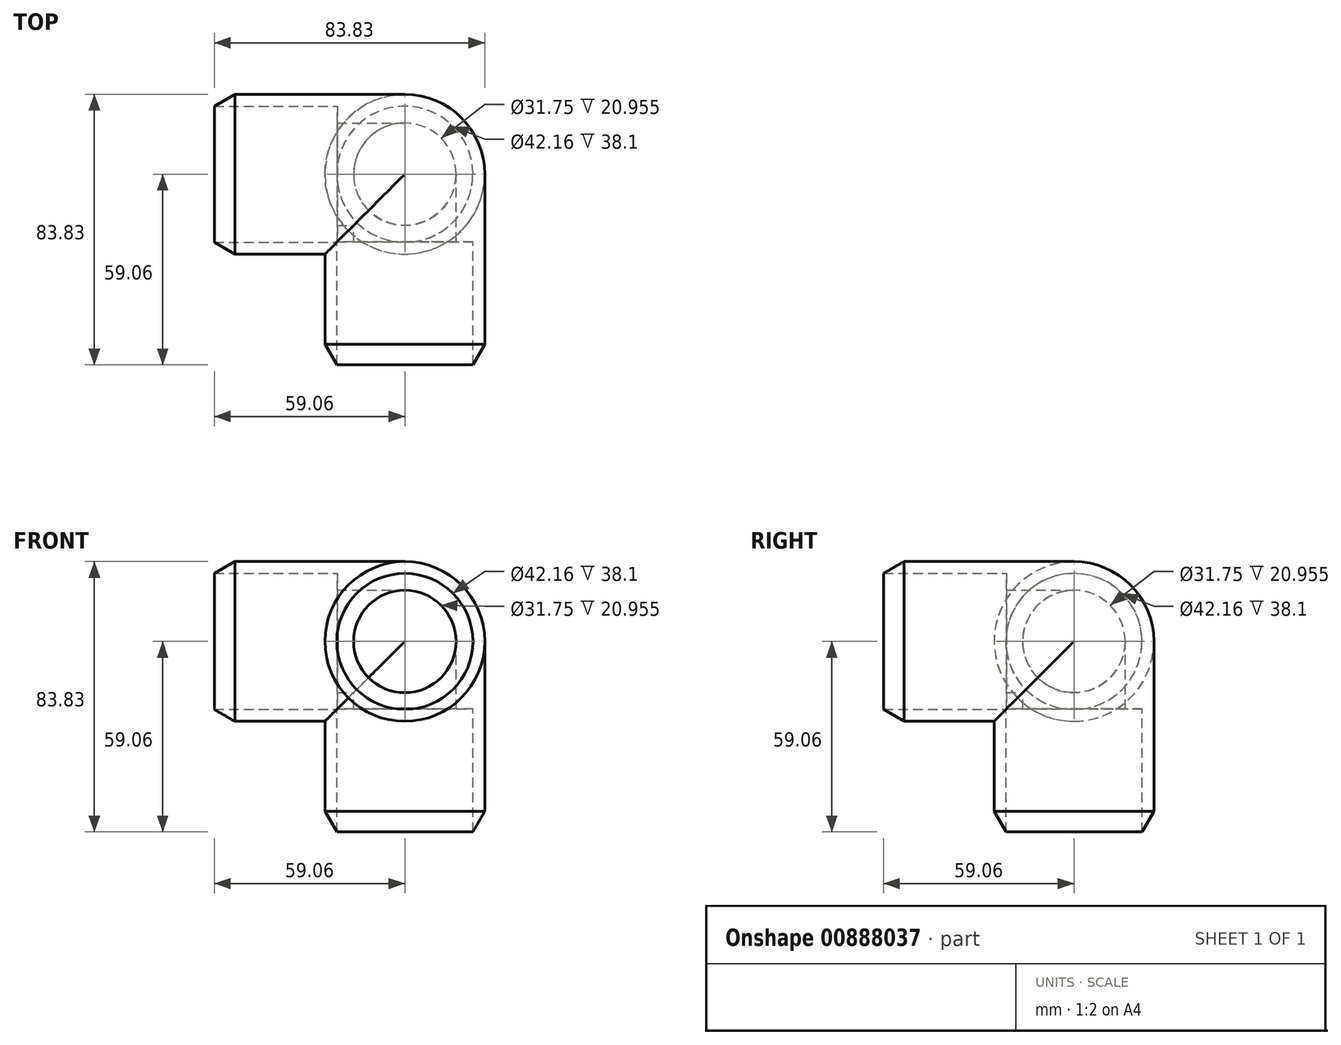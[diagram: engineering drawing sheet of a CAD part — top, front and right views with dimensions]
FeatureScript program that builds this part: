
annotation { "Feature Type Name" : "Feature", "Feature Type Description" : "" }
export const myFeature = defineFeature(function(context is Context, id is Id, definition is map)
    precondition{}
    {
        {
            var Q0;
            Q0=qCreatedBy(makeId("Right.planeOp"),FACE);
            var sketch = newSketch(context, id + "F0", { "sketchPlane" : qUnion([Q0])});
            skLineSegment(sketch, "E0", {"start": v(-59.06, 21.08) * mm, "end": v(-20.96, 21.08) * mm});
            skLineSegment(sketch, "E1", {"start": v(-20.96, 21.08) * mm, "end": v(-20.96, 15.88) * mm});
            skLineSegment(sketch, "E2", {"start": v(-20.96, 15.88) * mm, "end": v(0, 15.88) * mm});
            skLineSegment(sketch, "E3", {"start": v(15.87, 0) * mm, "end": v(15.87, 0) * mm});
            skLineSegment(sketch, "E4", {"start": v(15.87, 0) * mm, "end": v(24.77, 0) * mm});
            skLineSegment(sketch, "E5", {"start": v(24.77, 0) * mm, "end": v(24.77, 0) * mm});
            skLineSegment(sketch, "E6", {"start": v(0, 24.77) * mm, "end": v(-52.68, 24.76) * mm});
            skLineSegment(sketch, "E7", {"start": v(-52.68, 24.76) * mm, "end": v(-59.06, 21.08) * mm});
            skArc(sketch, "E8.filletArc", {"start": v(24.77, 0) * mm, "mid": v(17.51, 17.51) * mm, "end": v(0, 24.77) * mm});
            skArc(sketch, "E9.filletArc", {"start": v(15.88, 0) * mm, "mid": v(11.23, 11.23) * mm, "end": v(0, 15.88) * mm});
            skLineSegment(sketch, "E10", {"start": v(0, 0) * mm, "end": v(0, -11.7) * mm});
            skLineSegment(sketch, "E11", {"start": v(0, 0) * mm, "end": v(10.52, 0) * mm});
            skLineSegment(sketch, "E12", {"start": v(-59.06, 21.08) * mm, "end": v(-59.06, 0) * mm});
            skLineSegment(sketch, "E13", {"start": v(-59.06, 0) * mm, "end": v(15.87, 0) * mm});
            skSolve(sketch);
        }
        {
            var Q0;
            Q0=qCreatedBy(makeId("Right.planeOp"),FACE);
            var sketch = newSketch(context, id + "F1", { "sketchPlane" : qUnion([Q0])});
            skLineSegment(sketch, "E14", {"start": v(-21.08, -59.06) * mm, "end": v(-21.08, -20.96) * mm});
            skLineSegment(sketch, "E15", {"start": v(-21.08, -20.96) * mm, "end": v(-15.88, -20.96) * mm});
            skLineSegment(sketch, "E16", {"start": v(-15.88, -20.96) * mm, "end": v(-15.88, 0) * mm});
            skLineSegment(sketch, "E17", {"start": v(0, 15.88) * mm, "end": v(0, 15.88) * mm});
            skLineSegment(sketch, "E18", {"start": v(0, 15.88) * mm, "end": v(0, 24.77) * mm});
            skLineSegment(sketch, "E19", {"start": v(0, 24.77) * mm, "end": v(0, 24.77) * mm});
            skLineSegment(sketch, "E20", {"start": v(-24.77, 0) * mm, "end": v(-24.76, -52.68) * mm});
            skLineSegment(sketch, "E21", {"start": v(-24.76, -52.68) * mm, "end": v(-21.08, -59.06) * mm});
            skArc(sketch, "E22.filletArc", {"start": v(0, 24.77) * mm, "mid": v(-17.51, 17.51) * mm, "end": v(-24.77, 0) * mm});
            skArc(sketch, "E23.filletArc", {"start": v(0, 15.88) * mm, "mid": v(-11.23, 11.23) * mm, "end": v(-15.88, 0) * mm});
            skLineSegment(sketch, "E24", {"start": v(0, 36.04) * mm, "end": v(0, 0) * mm});
            skLineSegment(sketch, "E25", {"start": v(-2.18, 0) * mm, "end": v(0, 0) * mm});
            skLineSegment(sketch, "E26", {"start": v(-21.08, -59.06) * mm, "end": v(0, -59.06) * mm});
            skLineSegment(sketch, "E27", {"start": v(0, -59.06) * mm, "end": v(0, 15.88) * mm});
            skSolve(sketch);
        }
        {
            var Q0;
            Q0=qCreatedBy(makeId("Top.planeOp"),FACE);
            var sketch = newSketch(context, id + "F2", { "sketchPlane" : qUnion([Q0])});
            skLineSegment(sketch, "E28", {"start": v(-59.06, 21.08) * mm, "end": v(-20.96, 21.08) * mm});
            skLineSegment(sketch, "E29", {"start": v(-20.96, 21.08) * mm, "end": v(-20.96, 15.88) * mm});
            skLineSegment(sketch, "E30", {"start": v(-20.96, 15.88) * mm, "end": v(0, 15.88) * mm});
            skLineSegment(sketch, "E31", {"start": v(15.88, 0) * mm, "end": v(15.88, 0) * mm});
            skLineSegment(sketch, "E32", {"start": v(15.88, 0) * mm, "end": v(24.77, 0) * mm});
            skLineSegment(sketch, "E33", {"start": v(24.77, 0) * mm, "end": v(24.77, 0) * mm});
            skLineSegment(sketch, "E34", {"start": v(0, 24.77) * mm, "end": v(-52.68, 24.76) * mm});
            skLineSegment(sketch, "E35", {"start": v(-52.68, 24.76) * mm, "end": v(-59.06, 21.08) * mm});
            skArc(sketch, "E36.filletArc", {"start": v(24.77, 0) * mm, "mid": v(17.51, 17.51) * mm, "end": v(0, 24.77) * mm});
            skArc(sketch, "E37.filletArc", {"start": v(15.88, 0) * mm, "mid": v(11.23, 11.23) * mm, "end": v(0, 15.88) * mm});
            skLineSegment(sketch, "E38", {"start": v(0, 15.42) * mm, "end": v(0, 0) * mm});
            skLineSegment(sketch, "E39", {"start": v(-12.56, 0) * mm, "end": v(0, 0) * mm});
            skLineSegment(sketch, "E40", {"start": v(-59.06, 21.08) * mm, "end": v(-59.06, 0) * mm});
            skLineSegment(sketch, "E41", {"start": v(-59.06, 0) * mm, "end": v(15.87, 0) * mm});
            skSolve(sketch);
        }
        {
            var Q0;
            Q0 = qSketchRegion(id + "F0", true);
            var Q1;
            Q1=sQuery(id+"F0.wireOp",EDGE,"E13");
            revolve(context, id + "F3", {"surfaceOperationType" : NewSurfaceOperationType.NEW, "entities" : qUnion([Q0]), "axis" : qUnion([Q1]), "revolveType" : RevolveType.FULL});
        }
        {
            var Q0;
            Q0 = qSketchRegion(id + "F1", true);
            var Q1;
            Q1=sQuery(id+"F1.wireOp",EDGE,"E27");
            revolve(context, id + "F4", {"operationType" : NewBodyOperationType.ADD, "surfaceOperationType" : NewSurfaceOperationType.NEW, "entities" : qUnion([Q0]), "axis" : qUnion([Q1]), "revolveType" : RevolveType.FULL});
        }
        {
            var Q0;
            Q0 = qSketchRegion(id + "F2", true);
            var Q1;
            Q1=sQuery(id+"F2.wireOp",EDGE,"E41");
            revolve(context, id + "F5", {"operationType" : NewBodyOperationType.ADD, "surfaceOperationType" : NewSurfaceOperationType.NEW, "entities" : qUnion([Q0]), "axis" : qUnion([Q1]), "revolveType" : RevolveType.FULL});
        }
        {
            var Q0;
            Q0=makeQuery(id+"F0.imprint","IMPRINT",FACE,{"disambiguationData":[TD([[makeQuery(id+"F0.imprint","IMPRINT",EDGE,{"derivedFrom":sQuery(id+"F0.wireOp",EDGE,"E0")}),-1.0]])]});
            var Q1;
            Q1=sQuery(id+"F0.wireOp",EDGE,"E13");
            revolve(context, id + "F6", {"operationType" : NewBodyOperationType.REMOVE, "surfaceOperationType" : NewSurfaceOperationType.NEW, "entities" : qUnion([Q0]), "axis" : qUnion([Q1]), "revolveType" : RevolveType.FULL, "oppositeDirection" : true});
        }
        {
            var Q0;
            Q0=makeQuery(id+"F1.imprint","IMPRINT",FACE,{"disambiguationData":[TD([[makeQuery(id+"F1.imprint","IMPRINT",EDGE,{"derivedFrom":sQuery(id+"F1.wireOp",EDGE,"E14")}),-1.0]])]});
            var Q1;
            Q1=sQuery(id+"F1.wireOp",EDGE,"E27");
            revolve(context, id + "F7", {"operationType" : NewBodyOperationType.REMOVE, "surfaceOperationType" : NewSurfaceOperationType.NEW, "entities" : qUnion([Q0]), "axis" : qUnion([Q1]), "revolveType" : RevolveType.FULL, "oppositeDirection" : true});
        }
        {
            var Q0;
            Q0=makeQuery(id+"F2.imprint","IMPRINT",FACE,{"disambiguationData":[TD([[makeQuery(id+"F2.imprint","IMPRINT",EDGE,{"derivedFrom":sQuery(id+"F2.wireOp",EDGE,"E28")}),-1.0]])]});
            var Q1;
            Q1=sQuery(id+"F2.wireOp",EDGE,"E41");
            revolve(context, id + "F8", {"operationType" : NewBodyOperationType.REMOVE, "surfaceOperationType" : NewSurfaceOperationType.NEW, "entities" : qUnion([Q0]), "axis" : qUnion([Q1]), "revolveType" : RevolveType.FULL, "oppositeDirection" : true});
        }
    });
